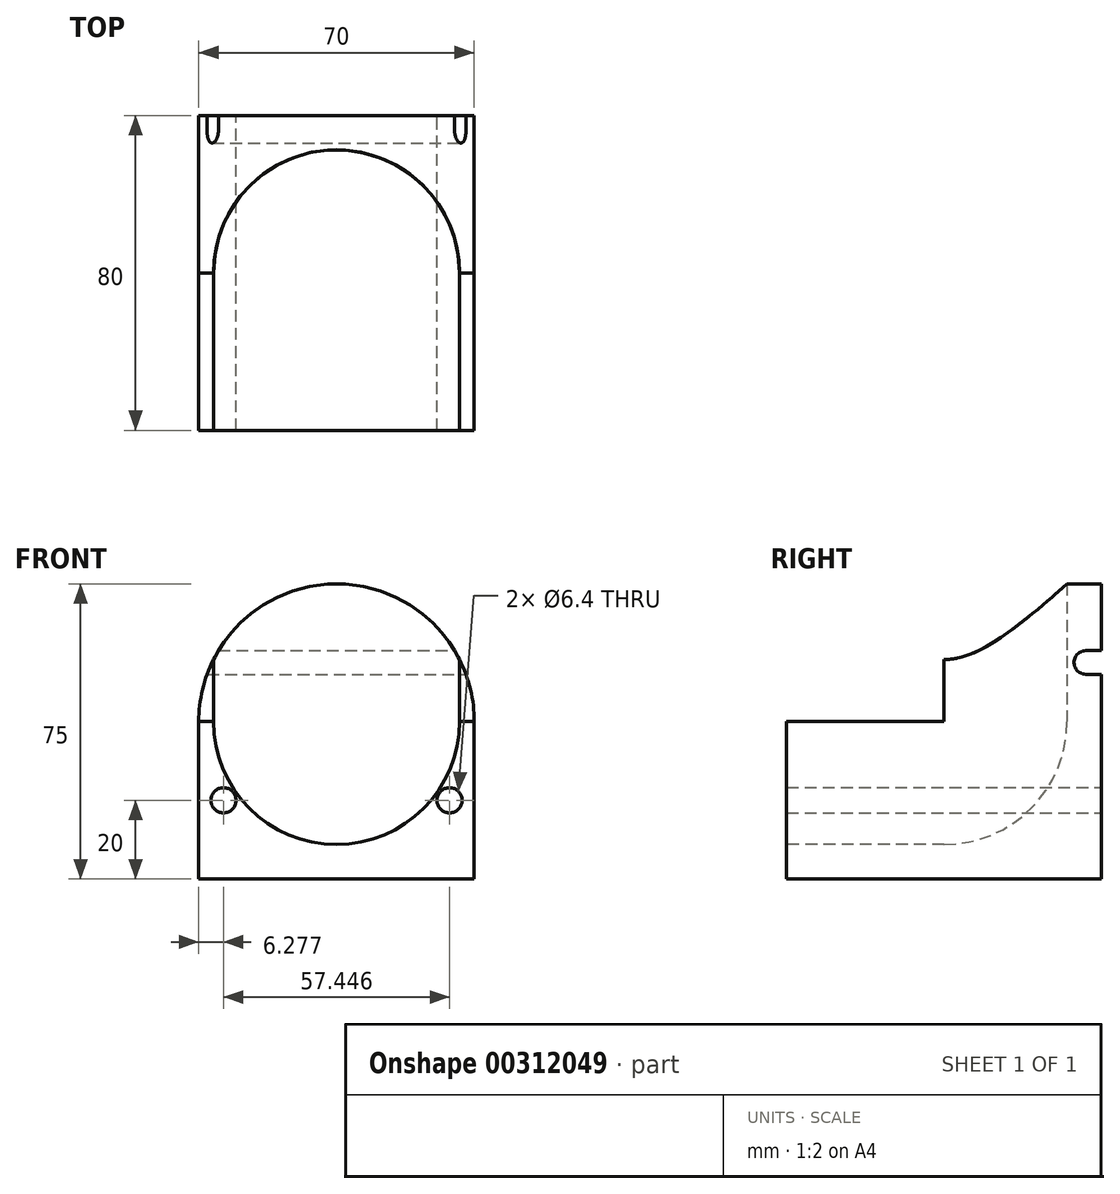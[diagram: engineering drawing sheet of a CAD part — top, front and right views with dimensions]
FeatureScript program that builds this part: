
annotation { "Feature Type Name" : "Feature", "Feature Type Description" : "" }
export const myFeature = defineFeature(function(context is Context, id is Id, definition is map)
    precondition{}
    {
        {
            var Q0;
            Q0=qCreatedBy(makeId("Front.planeOp"),FACE);
            var sketch = newSketch(context, id + "F0", { "sketchPlane" : qUnion([Q0])});
            skCircle(sketch, "E0", {"center": v(0, 0) * mm, "radius": 35 * mm});
            skLineSegment(sketch, "E1", {"start": v(-35, 0) * mm, "end": v(-35, -40) * mm});
            skLineSegment(sketch, "E2", {"start": v(-35, -40) * mm, "end": v(35, -40) * mm});
            skLineSegment(sketch, "E3", {"start": v(35, -40) * mm, "end": v(35, 0) * mm});
            skCircle(sketch, "E4", {"center": v(-28.72, -20) * mm, "radius": 3.2 * mm});
            skCircle(sketch, "E5", {"center": v(28.72, -20) * mm, "radius": 3.2 * mm});
            skLineSegment(sketch, "E6", {"start": v(-28.72, -20) * mm, "end": v(-28.72, -40) * mm, "construction": true});
            skLineSegment(sketch, "E7", {"start": v(28.72, -20) * mm, "end": v(28.72, -40) * mm, "construction": true});
            skLineSegment(sketch, "E8", {"start": v(28.72, -20) * mm, "end": v(-28.72, -20) * mm, "construction": true});
            skSolve(sketch);
        }
        {
            var Q0;
            Q0 = qSketchRegion(id + "F0", true);
            extrude(context, id + "F1", {"entities" : qUnion([Q0]), "depth" : 80 * mm});
        }
        {
            var Q0;
            Q0=makeQuery(id+"F1.opExtrude","CAP_FACE",FACE,{"disambiguationData":[OSD([sQuery(id+"F0.wireOp",EDGE,"E0"),sQuery(id+"F0.wireOp",EDGE,"E1"),sQuery(id+"F0.wireOp",EDGE,"E2"),sQuery(id+"F0.wireOp",EDGE,"E3"),sQuery(id+"F0.wireOp",EDGE,"E4"),sQuery(id+"F0.wireOp",EDGE,"E5")])],"isStart":false});
            var sketch = newSketch(context, id + "F2", { "sketchPlane" : qUnion([Q0])});
            skCircle(sketch, "E9", {"center": v(0, 0) * mm, "radius": 31.25 * mm});
            skLineSegment(sketch, "E10", {"start": v(-31.25, 0) * mm, "end": v(-35, 0) * mm});
            skLineSegment(sketch, "E11", {"start": v(31.25, 0) * mm, "end": v(35, 0) * mm});
            skArc(sketch, "E12.0", {"start": v(35, 0) * mm, "mid": v(0, 35) * mm, "end": v(-35, 0) * mm});
            skSolve(sketch);
        }
        {
            var Q0;
            Q0 = qSketchRegion(id + "F2", true);
            extrude(context, id + "F3", {"entities" : qUnion([Q0]), "operationType" : NewBodyOperationType.REMOVE, "oppositeDirection" : true, "depth" : 40 * mm});
        }
        {
            var Q0;
            Q0=makeQuery(id+"F3.boolean.opBoolean","COPY",FACE,{"derivedFrom":makeQuery(id+"F3.opExtrude","SWEPT_FACE",FACE,{"disambiguationData":[OSD([sQuery(id+"F2.wireOp",EDGE,"E10")])]})});
            cPlane(context, id + "F4", {"entities" : qUnion([Q0]), "cplaneType" : CPlaneType.OFFSET, "offset" : 0 * mm, "width" : 150 * mm, "height" : 150 * mm});
        }
        {
            var Q0;
            Q0=qCreatedBy(id+"F4.planeOp",FACE);
            var sketch = newSketch(context, id + "F5", { "sketchPlane" : qUnion([Q0])});
            skPoint(sketch, "E13.0", {"position": v(0, -40) * mm});
            skPoint(sketch, "E14.0", {"position": v(-31.25, -40) * mm});
            skPoint(sketch, "E15.0", {"position": v(31.25, -40) * mm});
            skCircle(sketch, "E16", {"center": v(0, -40) * mm, "radius": 31.25 * mm});
            skSolve(sketch);
        }
        {
            var Q0;
            Q0 = qSketchRegion(id + "F5", true);
            extrude(context, id + "F6", {"entities" : qUnion([Q0]), "operationType" : NewBodyOperationType.REMOVE, "depth" : 50.2 * mm});
        }
        {
            var Q0;
            Q0=makeQuery(id+"F6.boolean.opBoolean","COPY",FACE,{"derivedFrom":makeQuery(id+"F6.opExtrude","CAP_FACE",FACE,{"disambiguationData":[OSD([sQuery(id+"F5.wireOp",EDGE,"E16")])],"isStart":true})});
            var Q1;
            Q1=makeQuery(id+"F6.boolean.opBoolean","COPY",EDGE,{"derivedFrom":makeQuery(id+"F6.opExtrude","CAP_EDGE",EDGE,{"disambiguationData":[OSD([sQuery(id+"F5.wireOp",EDGE,"E16")])],"isStart":true})});
            var Q2;
            Q2=makeQuery(id+"F6.boolean.opBoolean","INTERSECT",EDGE,{"derivedFrom":[makeQuery(id+"F3.boolean.opBoolean","COPY",FACE,{"derivedFrom":makeQuery(id+"F3.opExtrude","CAP_FACE",FACE,{"disambiguationData":[OSD([sQuery(id+"F2.wireOp",EDGE,"E9"),sQuery(id+"F2.wireOp",EDGE,"E10"),sQuery(id+"F2.wireOp",EDGE,"E11"),sQuery(id+"F2.wireOp",EDGE,"E12.0")])],"isStart":false})}),makeQuery(id+"F6.opExtrude","CAP_FACE",FACE,{"disambiguationData":[OSD([sQuery(id+"F5.wireOp",EDGE,"E16")])],"isStart":true})]});
            revolve(context, id + "F7", {"operationType" : NewBodyOperationType.REMOVE, "entities" : qUnion([Q0]), "surfaceEntities" : qUnion([Q1]), "axis" : qUnion([Q2]), "revolveType" : RevolveType.ONE_DIRECTION, "angle" : 90 * degree});
        }
        {
            var Q0;
            Q0=makeQuery(id+"F1.opExtrude","CAP_FACE",FACE,{"disambiguationData":[OSD([sQuery(id+"F0.wireOp",EDGE,"E0"),sQuery(id+"F0.wireOp",EDGE,"E1"),sQuery(id+"F0.wireOp",EDGE,"E2"),sQuery(id+"F0.wireOp",EDGE,"E3"),sQuery(id+"F0.wireOp",EDGE,"E4"),sQuery(id+"F0.wireOp",EDGE,"E5")])],"isStart":true});
            var sketch = newSketch(context, id + "F8", { "sketchPlane" : qUnion([Q0])});
            skLineSegment(sketch, "E17", {"start": v(0, -40) * mm, "end": v(0, 35) * mm, "construction": true});
            skLineSegment(sketch, "E18", {"start": v(-35, 0) * mm, "end": v(35, 0) * mm, "construction": true});
            skLineSegment(sketch, "E19", {"start": v(0, 0) * mm, "end": v(0, 15) * mm});
            skLineSegment(sketch, "E20", {"start": v(0, 15) * mm, "end": v(-31.62, 15) * mm});
            skLineSegment(sketch, "E21", {"start": v(0, 15) * mm, "end": v(31.62, 15) * mm});
            skPoint(sketch, "E22.middle", {"position": v(0, 15) * mm});
            skLineSegment(sketch, "E23.bottom", {"start": v(-32.88, 12) * mm, "end": v(32.88, 12) * mm});
            skLineSegment(sketch, "E23.top", {"start": v(-32.88, 18) * mm, "end": v(32.88, 18) * mm});
            skLineSegment(sketch, "E23.left", {"start": v(-32.88, 12) * mm, "end": v(-32.88, 18) * mm});
            skLineSegment(sketch, "E23.right", {"start": v(32.88, 12) * mm, "end": v(32.88, 18) * mm});
            skSolve(sketch);
        }
        {
            var Q0;
            Q0 = qSketchRegion(id + "F8", true);
            extrude(context, id + "F9", {"entities" : qUnion([Q0]), "operationType" : NewBodyOperationType.REMOVE, "oppositeDirection" : true, "depth" : 4 * mm});
        }
        {
            var Q0;
            Q0 = qSketchRegion(id + "F8", true);
            extrude(context, id + "F10", {"entities" : qUnion([Q0]), "operationType" : NewBodyOperationType.ADD, "oppositeDirection" : true, "depth" : 4 * mm});
        }
        {
            var Q0;
            Q0=makeQuery(id+"F10.opExtrude","SWEPT_FACE",FACE,{"disambiguationData":[OSD([sQuery(id+"F8.wireOp",EDGE,"E23.left")])]});
            var sketch = newSketch(context, id + "F11", { "sketchPlane" : qUnion([Q0])});
            skArc(sketch, "E24", {"start": v(-4, 12) * mm, "mid": v(-7, 15) * mm, "end": v(-4, 18) * mm});
            skLineSegment(sketch, "E25", {"start": v(-4, 18) * mm, "end": v(0, 18) * mm});
            skLineSegment(sketch, "E26", {"start": v(0, 18) * mm, "end": v(0, 12) * mm});
            skLineSegment(sketch, "E27", {"start": v(0, 12) * mm, "end": v(-4, 12) * mm});
            skSolve(sketch);
        }
        {
            var Q0;
            Q0 = qSketchRegion(id + "F11", true);
            extrude(context, id + "F12", {"entities" : qUnion([Q0]), "operationType" : NewBodyOperationType.REMOVE, "endBound" : BoundingType.THROUGH_ALL, "oppositeDirection" : true, "depth" : 25 * mm});
        }
    });
